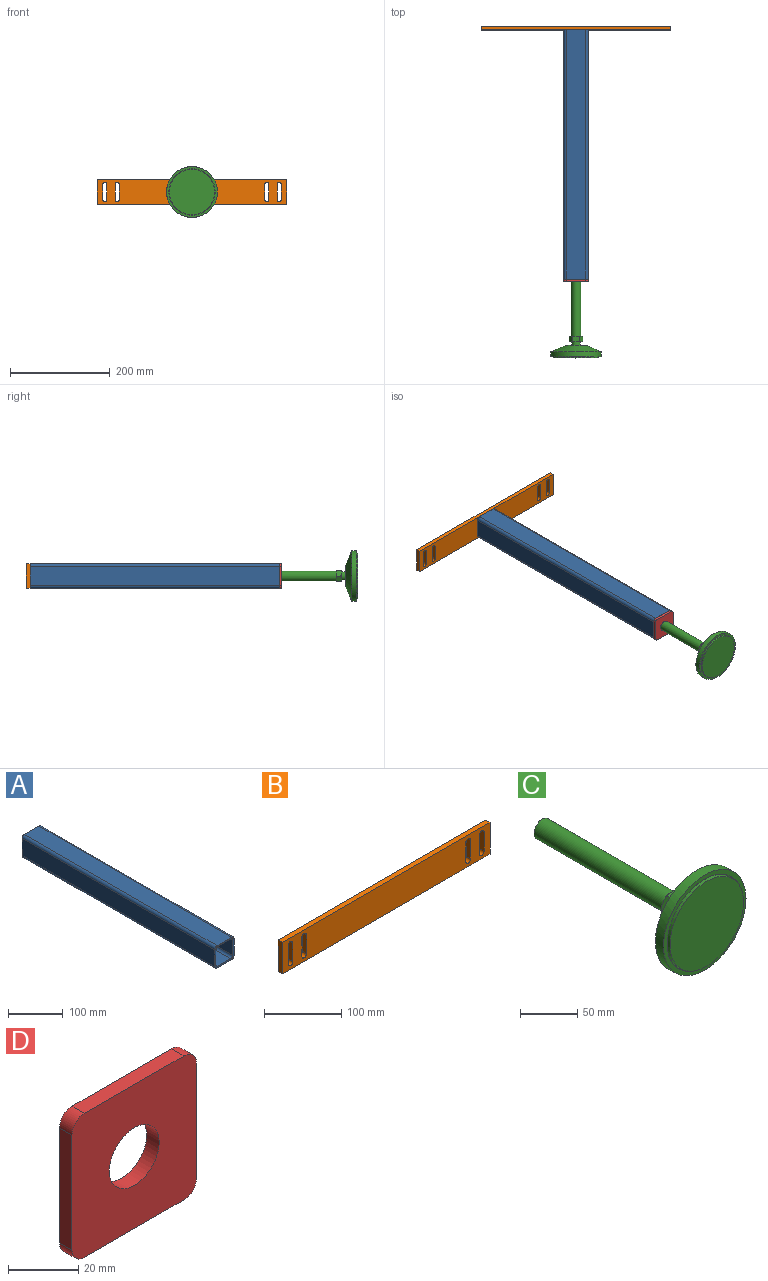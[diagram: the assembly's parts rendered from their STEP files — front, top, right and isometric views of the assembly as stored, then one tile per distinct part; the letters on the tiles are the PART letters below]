
ASSEMBLY  parts=4 mates=3
PART A: 18 faces, bbox 50x500x50 mm
  f0: plane 500x38mm, normal (0,0,-1), area 19000mm2, adj f4,f5,f14,f17
  f1: plane 500x38mm, normal (1,0,0), area 19000mm2, adj f4,f5,f14,f15
  f2: plane 500x38mm, normal (0,0,1), area 19000mm2, adj f4,f5,f15,f16
  f3: plane 500x38mm, normal (-1,0,0), area 19000mm2, adj f4,f5,f16,f17
  f4: plane 50x50mm, normal (0,-1,0), area 554.6mm2, adj f0,f1,f2,f3,f6,f7,f8,f9
  f5: plane 50x50mm, normal (0,1,0), area 554.6mm2, adj f0,f1,f2,f3,f6,f7,f8,f9
  f6: plane 500x34mm, normal (0,0,-1), area 17000mm2, adj f4,f5,f7,f13
  f7: cylinder r=5mm len=500mm, axis (0,-1,0), area 3927mm2, adj f4,f5,f6,f8
  f8: plane 500x34mm, normal (1,0,0), area 17000mm2, adj f4,f5,f7,f9
  f9: cylinder r=5mm len=500mm, axis (0,-1,0), area 3927mm2, adj f4,f5,f8,f10
  f10: plane 500x34mm, normal (0,0,1), area 17000mm2, adj f4,f5,f9,f11
  f11: cylinder r=5mm len=500mm, axis (0,-1,0), area 3927mm2, adj f4,f5,f10,f12
  f12: plane 500x34mm, normal (-1,0,0), area 17000mm2, adj f4,f5,f11,f13
  f13: cylinder r=5mm len=500mm, axis (0,-1,0), area 3927mm2, adj f4,f5,f6,f12
  f14: cylinder r=6mm len=500mm, axis (0,-1,0), area 4712.4mm2, adj f0,f1,f4,f5
  f15: cylinder r=6mm len=500mm, axis (0,1,0), area 4712.4mm2, adj f1,f2,f4,f5
  f16: cylinder r=6mm len=500mm, axis (0,-1,0), area 4712.4mm2, adj f2,f3,f4,f5
  f17: cylinder r=6mm len=500mm, axis (0,1,0), area 4712.4mm2, adj f0,f3,f4,f5
PART B: 22 faces, bbox 380x8x50 mm
  f0: plane 380x8mm, normal (0,0,-1), area 3040mm2, adj f1,f3,f4,f5
  f1: plane 50x8mm, normal (1,0,0), area 400mm2, adj f0,f2,f4,f5
  f2: plane 380x8mm, normal (0,0,1), area 3040mm2, adj f1,f3,f4,f5
  f3: plane 50x8mm, normal (-1,0,0), area 400mm2, adj f0,f2,f4,f5
  f4: plane 380x50mm, normal (0,-1,0), area 17753mm2, adj f0,f1,f2,f3,f6,f7,f8,f9
  f5: plane 380x50mm, normal (0,1,0), area 17753mm2, adj f0,f1,f2,f3,f6,f7,f8,f9
  f6: plane 30x8mm, normal (-1,0,0), area 240mm2, adj f4,f5,f7,f9
  f7: cylinder r=4.25mm len=8.5mm, axis (0,1,0), area 106.8mm2, adj f4,f5,f6,f8
  f8: plane 30x8mm, normal (1,0,0), area 240mm2, adj f4,f5,f7,f9
  f9: cylinder r=4.25mm len=8.5mm, axis (0,1,0), area 106.8mm2, adj f4,f5,f6,f8
  f10: plane 30x8mm, normal (-1,0,0), area 240mm2, adj f4,f5,f11,f13
  f11: cylinder r=4.25mm len=8.5mm, axis (0,1,0), area 106.8mm2, adj f4,f5,f10,f12
  f12: plane 30x8mm, normal (1,0,0), area 240mm2, adj f4,f5,f11,f13
  f13: cylinder r=4.25mm len=8.5mm, axis (0,1,0), area 106.8mm2, adj f4,f5,f10,f12
  f14: plane 30x8mm, normal (-1,0,0), area 240mm2, adj f4,f5,f15,f17
  f15: cylinder r=4.25mm len=8.5mm, axis (0,1,0), area 106.8mm2, adj f4,f5,f14,f16
  f16: plane 30x8mm, normal (1,0,0), area 240mm2, adj f4,f5,f15,f17
  f17: cylinder r=4.25mm len=8.5mm, axis (0,1,0), area 106.8mm2, adj f4,f5,f14,f16
  f18: plane 30x8mm, normal (-1,0,0), area 240mm2, adj f4,f5,f19,f21
  f19: cylinder r=4.25mm len=8.5mm, axis (0,1,0), area 106.8mm2, adj f4,f5,f18,f20
  f20: plane 30x8mm, normal (1,0,0), area 240mm2, adj f4,f5,f19,f21
  f21: cylinder r=4.25mm len=8.5mm, axis (0,1,0), area 106.8mm2, adj f4,f5,f18,f20
PART C: 31 faces, bbox 103.2x204.7x103.2 mm
  f0: plane 15.1x11.72mm, normal (0,0,-1), area 141.6mm2, adj f1,f2,f7,f8,f9,f27,f28,f30
  f1: torus R=12.38mm, axis (0,1,0), area 8.7mm2, adj f0,f2,f9
  f2: plane 13.24x11.72mm, normal (0.87,0,-0.5), area 141.1mm2, adj f0,f1,f5,f7,f9,f10,f26,f27
  f3: torus R=12.38mm, axis (0,1,0), area 8.7mm2, adj f5,f6,f7
  f4: plane 13.24x11.72mm, normal (-0.87,0,0.5), area 141.4mm2, adj f6,f7,f8,f9,f12,f13,f25,f29
  f5: plane 13.24x11.72mm, normal (0.87,0,0.5), area 141.5mm2, adj f2,f3,f6,f7,f9,f10,f11,f26
  f6: plane 15.1x11.72mm, normal (0,0,1), area 141.5mm2, adj f3,f4,f5,f7,f9,f11,f12,f25
  f7: plane 24.75x24.03mm, normal (0,1,0), area 158.4mm2, adj f0,f2,f3,f4,f5,f6,f8,f14
  f8: plane 13.24x11.72mm, normal (-0.87,0,-0.5), area 141.4mm2, adj f0,f4,f7,f9,f13,f28,f29,f30
  f9: plane 24.75x24.03mm, normal (0,-1,0), area 245.6mm2, adj f0,f1,f2,f4,f5,f6,f8,f10
  f10: torus R=12.38mm, axis (0,1,0), area 8.7mm2, adj f2,f5,f9
  f11: torus R=12.38mm, axis (0,1,0), area 8.7mm2, adj f5,f6,f9
  f12: torus R=12.38mm, axis (0,1,0), area 8.7mm2, adj f4,f6,f9
  f13: torus R=12.38mm, axis (0,1,0), area 8.7mm2, adj f4,f8,f9
  f14: cylinder r=10mm len=160mm, axis (0,-1,0), area 10053.1mm2, adj f7,f15
  f15: plane 20x20mm, normal (0,1,0), area 314.2mm2, adj f14
  f16: plane 42x42mm, normal (0,1,0), area 1158.5mm2, adj f19,f24
  f17: plane 91x91mm, normal (0,-1,0), area 6503.9mm2, adj f20
  f18: cylinder r=51mm len=102mm, axis (0,-1,0), area 3204.4mm2, adj f19,f21
  f19: cone r=21mm half-angle=67.4deg, axis (0,-1,0), area 7351.3mm2, adj f16,f18
  f20: cylinder r=45.5mm len=91mm, axis (0,-1,0), area 1000.6mm2, adj f17,f23
  f21: plane 102x102mm, normal (0,-1,0), area 1378.4mm2, adj f18,f22
  f22: cylinder r=46.5mm len=93mm, axis (0,-1,0), area 292.2mm2, adj f21,f23
  f23: plane 93x93mm, normal (0,-1,0), area 289mm2, adj f20,f22
  f24: cylinder r=8.5mm len=17mm, axis (0,-1,0), area 427.3mm2, adj f9,f16
  f25: torus R=12.38mm, axis (0,1,0), area 8.7mm2, adj f4,f6,f7
  f26: torus R=12.38mm, axis (0,1,0), area 8.7mm2, adj f2,f5,f7
  f27: torus R=12.38mm, axis (0,1,0), area 8.7mm2, adj f0,f2,f7
  f28: torus R=12.38mm, axis (0,1,0), area 8.7mm2, adj f0,f7,f8
  f29: torus R=12.38mm, axis (0,1,0), area 8.7mm2, adj f4,f7,f8
  f30: torus R=12.38mm, axis (0,1,0), area 8.7mm2, adj f0,f8,f9
PART D: 11 faces, bbox 50x5x50 mm
  f0: plane 40x5mm, normal (0,0,-1), area 200mm2, adj f4,f5,f6,f9
  f1: plane 40x5mm, normal (1,0,0), area 200mm2, adj f4,f5,f6,f7
  f2: plane 40x5mm, normal (0,0,1), area 200mm2, adj f4,f5,f7,f8
  f3: plane 40x5mm, normal (-1,0,0), area 200mm2, adj f4,f5,f8,f9
  f4: plane 50x50mm, normal (0,-1,0), area 2164.4mm2, adj f0,f1,f2,f3,f6,f7,f8,f9
  f5: plane 50x50mm, normal (0,1,0), area 2164.4mm2, adj f0,f1,f2,f3,f6,f7,f8,f9
  f6: cylinder r=5mm len=5mm, axis (0,-1,0), area 39.3mm2, adj f0,f1,f4,f5
  f7: cylinder r=5mm len=5mm, axis (0,1,0), area 39.3mm2, adj f1,f2,f4,f5
  f8: cylinder r=5mm len=5mm, axis (0,-1,0), area 39.3mm2, adj f2,f3,f4,f5
  f9: cylinder r=5mm len=5mm, axis (0,1,0), area 39.3mm2, adj f0,f3,f4,f5
  f10: cylinder r=10mm len=20mm, axis (0,-1,0), area 314.2mm2, adj f4,f5
PLACE A t=(-97.54,168.4,-37.93)mm fixed
PLACE B t=(-97.54,176.4,-37.93)mm
PLACE C t=(-97.54,-490.1,-37.93)mm
PLACE D t=(-97.54,-331.6,-37.93)mm fixed
MATE fastened C.f14 <-> D.f10  axis (0,-1,0) through (-97.54,-286.6,-37.93)mm
MATE fastened D.f5 <-> A.f4  axis (0,1,0) through (-97.54,-331.6,-12.93)mm
MATE fastened B.f4 <-> A.f5  axis (0,-1,0) through (-97.54,168.4,-37.93)mm
